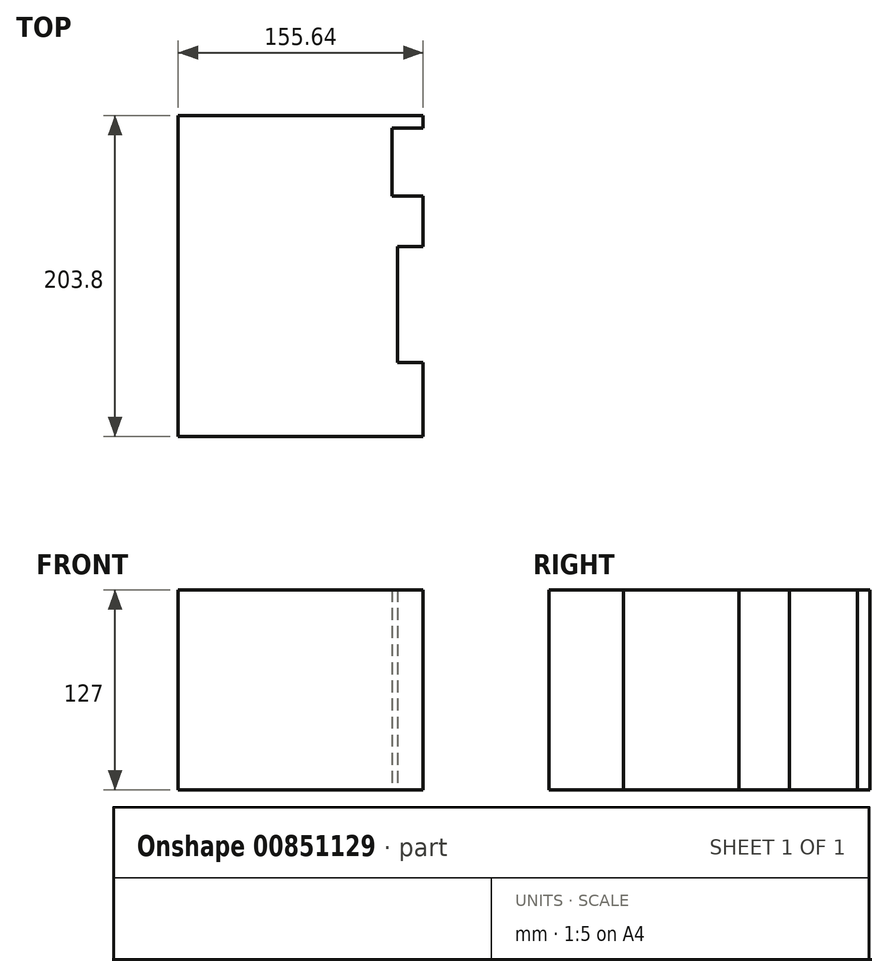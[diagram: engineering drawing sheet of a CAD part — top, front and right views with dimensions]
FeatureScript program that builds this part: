
annotation { "Feature Type Name" : "Feature", "Feature Type Description" : "" }
export const myFeature = defineFeature(function(context is Context, id is Id, definition is map)
    precondition{}
    {
        {
            var Q0;
            Q0=qCreatedBy(makeId("Top.planeOp"),FACE);
            var sketch = newSketch(context, id + "F0", { "sketchPlane" : qUnion([Q0])});
            skLineSegment(sketch, "E0.bottom", {"start": v(-42.59, -36.7) * mm, "end": v(42.59, -36.7) * mm});
            skLineSegment(sketch, "E0.top", {"start": v(-42.59, 36.7) * mm, "end": v(42.59, 36.7) * mm});
            skLineSegment(sketch, "E0.left", {"start": v(-42.59, -36.7) * mm, "end": v(-42.59, 36.7) * mm});
            skLineSegment(sketch, "E0.right", {"start": v(42.59, -36.7) * mm, "end": v(42.59, 36.7) * mm});
            skPoint(sketch, "E0.middle", {"position": v(0, 0) * mm});
            skLineSegment(sketch, "E1.bottom", {"start": v(-22.03, 112) * mm, "end": v(-45.88, 112) * mm});
            skLineSegment(sketch, "E1.top", {"start": v(-22.03, 68.8) * mm, "end": v(-45.88, 68.8) * mm});
            skLineSegment(sketch, "E1.left", {"start": v(-22.03, 112) * mm, "end": v(-22.03, 68.8) * mm});
            skLineSegment(sketch, "E1.right", {"start": v(-45.88, 112) * mm, "end": v(-45.88, 68.8) * mm});
            skPoint(sketch, "E1.middle", {"position": v(-33.95, 90.4) * mm});
            skLineSegment(sketch, "E2.bottom", {"start": v(-26.12, -83.82) * mm, "end": v(-181.76, -83.82) * mm});
            skLineSegment(sketch, "E2.top", {"start": v(-26.12, 119.98) * mm, "end": v(-181.76, 119.98) * mm});
            skLineSegment(sketch, "E2.left", {"start": v(-26.12, -83.82) * mm, "end": v(-26.12, 119.98) * mm});
            skLineSegment(sketch, "E2.right", {"start": v(-181.76, -83.82) * mm, "end": v(-181.76, 119.98) * mm});
            skPoint(sketch, "E2.middle", {"position": v(-103.94, 18.08) * mm});
            skSolve(sketch);
        }
        {
            var Q0;
            {var subQ9=sQuery(id+"F0.wireOp",EDGE,"E0.left");Q0=makeQuery(id+"F0.imprint","IMPRINT",FACE,{"disambiguationData":[TD([[makeQuery(id+"F0.imprint","IMPRINT",EDGE,{"derivedFrom":subQ9}),1.0]])]});}
            extrude(context, id + "F1", {"entities" : qUnion([Q0]), "depth" : 127 * mm, "offsetDistance" : 25.4 * mm});
        }
    });
